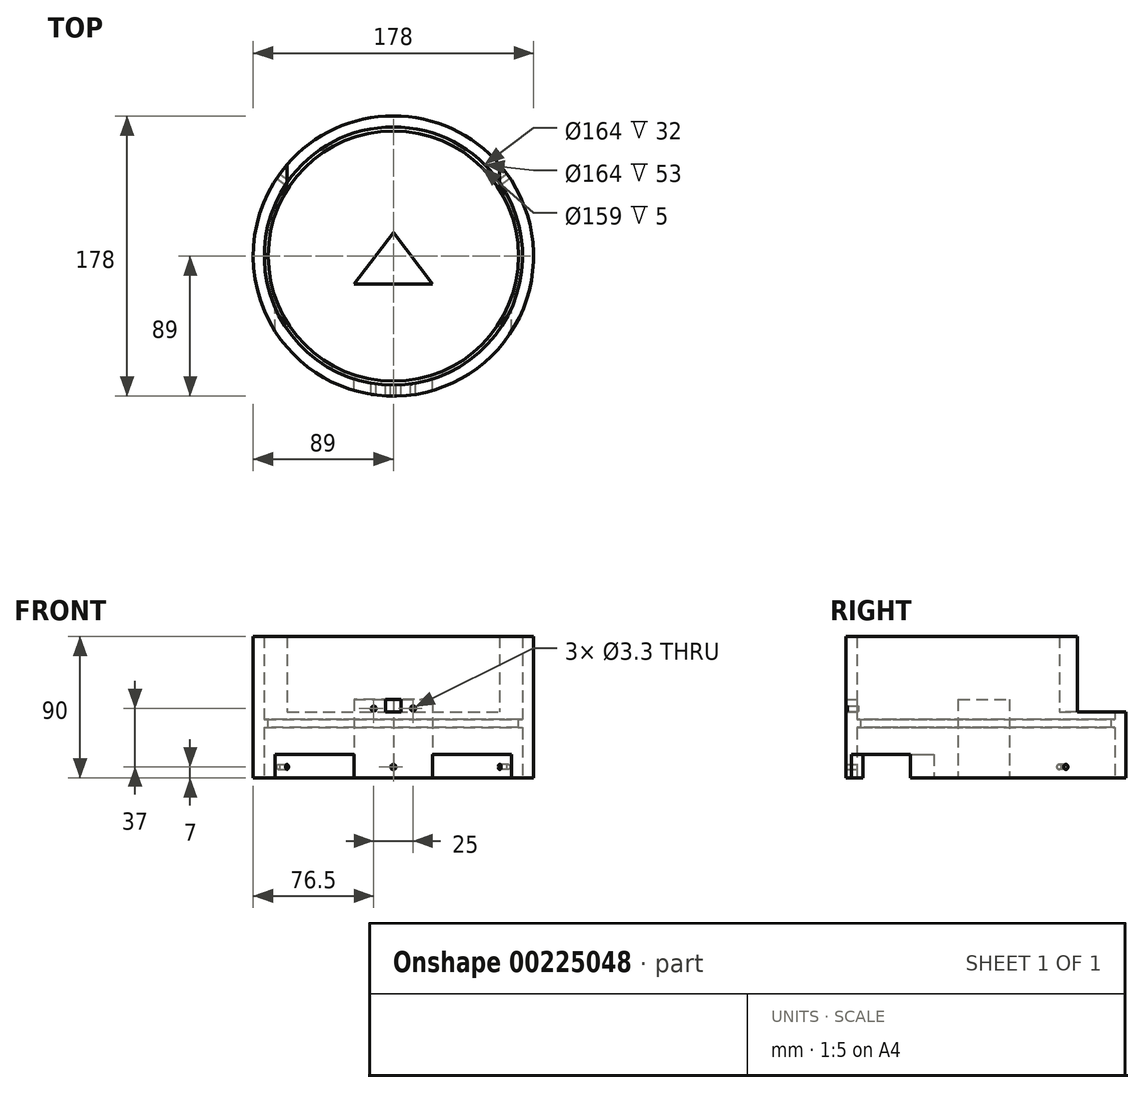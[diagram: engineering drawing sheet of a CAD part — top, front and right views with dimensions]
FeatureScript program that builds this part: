
annotation { "Feature Type Name" : "Feature", "Feature Type Description" : "" }
export const myFeature = defineFeature(function(context is Context, id is Id, definition is map)
    precondition{}
    {
        {
            var Q0;
            Q0=qCreatedBy(makeId("Top.planeOp"),FACE);
            var sketch = newSketch(context, id + "F0", { "sketchPlane" : qUnion([Q0])});
            skCircle(sketch, "E0", {"center": v(0, 0) * mm, "radius": 89 * mm});
            skCircle(sketch, "E1", {"center": v(0, 0) * mm, "radius": 82 * mm});
            skSolve(sketch);
        }
        {
            var Q0;
            Q0=qSketchRegion(id+"F0",true);
            extrude(context, id + "F1", {"entities" : qUnion([Q0]), "depth" : 90 * mm});
        }
        {
            var Q0;
            Q0=qCreatedBy(makeId("Front.planeOp"),FACE);
            var sketch = newSketch(context, id + "F2", { "sketchPlane" : qUnion([Q0])});
            skLineSegment(sketch, "E2.bottom", {"start": v(-67.5, 42) * mm, "end": v(67.5, 42) * mm});
            skLineSegment(sketch, "E2.top", {"start": v(-67.5, 90) * mm, "end": v(67.5, 90) * mm});
            skLineSegment(sketch, "E2.left", {"start": v(-67.5, 42) * mm, "end": v(-67.5, 90) * mm});
            skLineSegment(sketch, "E2.right", {"start": v(67.5, 42) * mm, "end": v(67.5, 90) * mm});
            skSolve(sketch);
        }
        {
            var Q0;
            Q0=qSketchRegion(id+"F2",true);
            extrude(context, id + "F3", {"entities" : qUnion([Q0]), "operationType" : NewBodyOperationType.REMOVE, "oppositeDirection" : true, "depth" : 130 * mm});
        }
        {
            var Q0;
            Q0=qCreatedBy(makeId("Front.planeOp"),FACE);
            var sketch = newSketch(context, id + "F4", { "sketchPlane" : qUnion([Q0])});
            skLineSegment(sketch, "E3.bottom", {"start": v(5, 50) * mm, "end": v(-5, 50) * mm});
            skLineSegment(sketch, "E3.top", {"start": v(5, 42) * mm, "end": v(-5, 42) * mm});
            skLineSegment(sketch, "E3.left", {"start": v(5, 50) * mm, "end": v(5, 42) * mm});
            skLineSegment(sketch, "E3.right", {"start": v(-5, 50) * mm, "end": v(-5, 42) * mm});
            skSolve(sketch);
        }
        {
            var Q0;
            Q0=qSketchRegion(id+"F4",true);
            extrude(context, id + "F5", {"entities" : qUnion([Q0]), "operationType" : NewBodyOperationType.REMOVE, "depth" : 100 * mm});
        }
        {
            var Q0;
            Q0=qCreatedBy(makeId("Front.planeOp"),FACE);
            var sketch = newSketch(context, id + "F6", { "sketchPlane" : qUnion([Q0])});
            skPoint(sketch, "E4", {"position": v(-12.5, 44) * mm});
            skPoint(sketch, "E5", {"position": v(12.5, 44) * mm});
            skPoint(sketch, "E6", {"position": v(0, 7) * mm});
            skSolve(sketch);
        }
        {
            var Q0;
            Q0=sQuery(id+"F6.wireOp",VERTEX,"E4");
            var Q1;
            Q1=sQuery(id+"F6.wireOp",VERTEX,"E5");
            var Q2;
            Q2=sQuery(id+"F6.wireOp",VERTEX,"E6");
            var Q3;
            Q3=makeQuery(id+"F1.opExtrude","SWEPT_BODY",BODY,{"disambiguationData":[OSD([sQuery(id+"F0.wireOp",EDGE,"E0"),sQuery(id+"F0.wireOp",EDGE,"E1")])]});
            hole(context, id + "F7", {"style" : HoleStyle.SIMPLE, "endStyle" : HoleEndStyle.THROUGH, "oppositeDirection" : true, "standardTappedOrClearance" : lookupTablePath({ "standard" : "ISO", "fit" : "Normal", "size" : "M3", "type" : "Clearance" }), "standardBlindInLast" : lookupTablePath({ "fit" : "Standard", "standard" : "ISO", "size" : "M3", "type" : "Clearance" }), "holeDiameter" : 3.3 * mm, "locations" : qUnion([Q0, Q1, Q2]), "scope" : qUnion([Q3]), "isTappedThrough" : true});
        }
        {
            var Q0;
            Q0=makeQuery(id+"F3.boolean.opBoolean","COPY",FACE,{"derivedFrom":makeQuery(id+"F3.opExtrude","SWEPT_FACE",FACE,{"disambiguationData":[OSD([sQuery(id+"F2.wireOp",EDGE,"E2.bottom")])]})});
            var sketch = newSketch(context, id + "F8", { "sketchPlane" : qUnion([Q0])});
            skCircle(sketch, "E7", {"center": v(0, 0) * mm, "radius": 82 * mm});
            skCircle(sketch, "E8", {"center": v(0, 0) * mm, "radius": 79.5 * mm});
            skSolve(sketch);
        }
        {
            var Q0;
            Q0 = qSketchRegion(id + "F8", true);
            extrude(context, id + "F9", {"entities" : qUnion([Q0]), "operationType" : NewBodyOperationType.ADD, "oppositeDirection" : true, "depth" : 10 * mm, "hasSecondDirection" : true, "secondDirectionOppositeDirection" : true, "secondDirectionDepth" : 5 * mm});
        }
        {
            var Q0;
            Q0=qCreatedBy(makeId("Front.planeOp"),FACE);
            var sketch = newSketch(context, id + "F10", { "sketchPlane" : qUnion([Q0])});
            skLineSegment(sketch, "E9.bottom", {"start": v(-25, 0) * mm, "end": v(-75, 0) * mm});
            skLineSegment(sketch, "E9.top", {"start": v(-25, 15) * mm, "end": v(-75, 15) * mm});
            skLineSegment(sketch, "E9.left", {"start": v(-25, 0) * mm, "end": v(-25, 15) * mm});
            skLineSegment(sketch, "E9.right", {"start": v(-75, 0) * mm, "end": v(-75, 15) * mm});
            skPoint(sketch, "E10.oppositeSnap0", {"position": v(-50, 15) * mm});
            skLineSegment(sketch, "E10.bottom", {"start": v(25, 0) * mm, "end": v(75, 0) * mm});
            skLineSegment(sketch, "E10.top", {"start": v(25, 15) * mm, "end": v(75, 15) * mm});
            skLineSegment(sketch, "E10.left", {"start": v(25, 0) * mm, "end": v(25, 15) * mm});
            skLineSegment(sketch, "E10.right", {"start": v(75, 0) * mm, "end": v(75, 15) * mm});
            skSolve(sketch);
        }
        {
            var Q0;
            Q0 = qSketchRegion(id + "F10", true);
            extrude(context, id + "F11", {"entities" : qUnion([Q0]), "operationType" : NewBodyOperationType.REMOVE, "depth" : 152.2 * mm});
        }
        {
            var Q0;
            Q0=qCreatedBy(makeId("Top.planeOp"),FACE);
            var sketch = newSketch(context, id + "F12", { "sketchPlane" : qUnion([Q0])});
            skLineSegment(sketch, "E11", {"start": v(-25, -17.68) * mm, "end": v(25, -17.68) * mm});
            skLineSegment(sketch, "E12", {"start": v(25, -17.68) * mm, "end": v(0, 14.9) * mm});
            skLineSegment(sketch, "E13", {"start": v(0, 14.9) * mm, "end": v(-25, -17.68) * mm});
            skLineSegment(sketch, "E14", {"start": v(0, 14.9) * mm, "end": v(0, -14.9) * mm});
            skSolve(sketch);
        }
        {
            var Q0;
            Q0 = qSketchRegion(id + "F12", true);
            extrude(context, id + "F13", {"entities" : qUnion([Q0]), "depth" : 50 * mm});
        }
        {
            var Q0;
            Q0=makeQuery(id+"F13.opExtrude","SWEPT_FACE",FACE,{"disambiguationData":[OSD([sQuery(id+"F12.wireOp",EDGE,"E13")])]});
            var sketch = newSketch(context, id + "F14", { "sketchPlane" : qUnion([Q0])});
            skPoint(sketch, "E15", {"position": v(4.25, 7) * mm});
            skSolve(sketch);
        }
        {
            var Q0;
            Q0=sQuery(id+"F14.wireOp",VERTEX,"E15");
            var Q1;
            Q1=makeQuery(id+"F1.opExtrude","SWEPT_BODY",BODY,{"disambiguationData":[OSD([sQuery(id+"F0.wireOp",EDGE,"E0"),sQuery(id+"F0.wireOp",EDGE,"E1")])]});
            hole(context, id + "F15", {"style" : HoleStyle.SIMPLE, "endStyle" : HoleEndStyle.THROUGH, "oppositeDirection" : true, "standardTappedOrClearance" : lookupTablePath({ "standard" : "ISO", "fit" : "Normal", "size" : "M3", "type" : "Clearance" }), "standardBlindInLast" : lookupTablePath({ "fit" : "Standard", "standard" : "ISO", "size" : "M3", "type" : "Clearance" }), "holeDiameter" : 3.3 * mm, "tappedDepth" : 12 * mm, "tapClearance" : 3, "locations" : qUnion([Q0]), "scope" : qUnion([Q1])});
        }
        {
            var Q0;
            Q0=makeQuery(id+"F13.opExtrude","SWEPT_FACE",FACE,{"disambiguationData":[OSD([sQuery(id+"F12.wireOp",EDGE,"E12")])]});
            var sketch = newSketch(context, id + "F16", { "sketchPlane" : qUnion([Q0])});
            skPoint(sketch, "E16", {"position": v(-4.25, 7) * mm});
            skSolve(sketch);
        }
        {
            var Q0;
            Q0=sQuery(id+"F16.wireOp",VERTEX,"E16");
            var Q1;
            Q1=makeQuery(id+"F1.opExtrude","SWEPT_BODY",BODY,{"disambiguationData":[OSD([sQuery(id+"F0.wireOp",EDGE,"E0"),sQuery(id+"F0.wireOp",EDGE,"E1")])]});
            hole(context, id + "F17", {"style" : HoleStyle.SIMPLE, "endStyle" : HoleEndStyle.THROUGH, "oppositeDirection" : true, "standardTappedOrClearance" : lookupTablePath({ "standard" : "ISO", "fit" : "Normal", "size" : "M3", "type" : "Clearance" }), "standardBlindInLast" : lookupTablePath({ "fit" : "Standard", "standard" : "ISO", "size" : "M3", "type" : "Clearance" }), "holeDiameter" : 3.3 * mm, "tappedDepth" : 12 * mm, "tapClearance" : 3, "locations" : qUnion([Q0]), "scope" : qUnion([Q1])});
        }
    });
